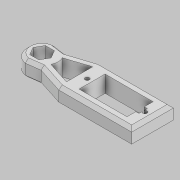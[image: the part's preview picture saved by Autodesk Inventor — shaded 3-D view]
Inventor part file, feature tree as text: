
AUTODESK INVENTOR PART (.ipt)
format: ipt  version: 2022.2 (Build 262287010, 287A)  size: 175,616 bytes
history: native  units: mm
features: extrude x3, sketch x3, chamfer x2, other x1, fillet x1
ambient origin geometry x8: Origin, YZ Plane, XZ Plane, XY Plane, X Axis, Y Axis, Z Axis, Center Point
bodies: Body1 (feature_tree)
feature tree (10):
  other  "Sólido1"
  extrude  "Extrusión1"  Depth=23.0mm
  extrude  "Extrusión2"  Depth=20.0mm
  extrude  "Extrusión3"  Depth=60.0mm
  chamfer  "Chaflán1"  Distance=7.5mm
  fillet  "Empalme1"  [1 undecoded]
  chamfer  "Chaflán2"  Distance=3.667mm
  sketch  "Boceto1"  dims[d1=35.0mm d2=23.0mm]
  sketch  "Boceto2"  dims[d3=12.5mm d4=20.0mm]
  sketch  "Boceto3"  dims[d6=14.0mm d7=60.0mm d8=7.5mm d9=0.0mm d10=3.667mm d11=0.0mm d13=8.0mm d14=0.0mm d15=6.0mm d16=6.0mm d17=30.0mm d18=30.0mm d19=2.0mm d20=2.0mm d21=27.7mm d22=0.0mm d23=0.0mm d24=4.0mm d25=0.0mm d26=0.0mm d27=1.5mm d28=2.0mm d29=45.0deg d30=6.0mm d31=1.5mm d32=2.0mm d33=45.0deg d34=1.5mm]
note: 1 required parameter value undecoded (feature->parameter linkage not recoverable at this tier; creation-order binding heuristic only, values carry confidence <= 0.55)
